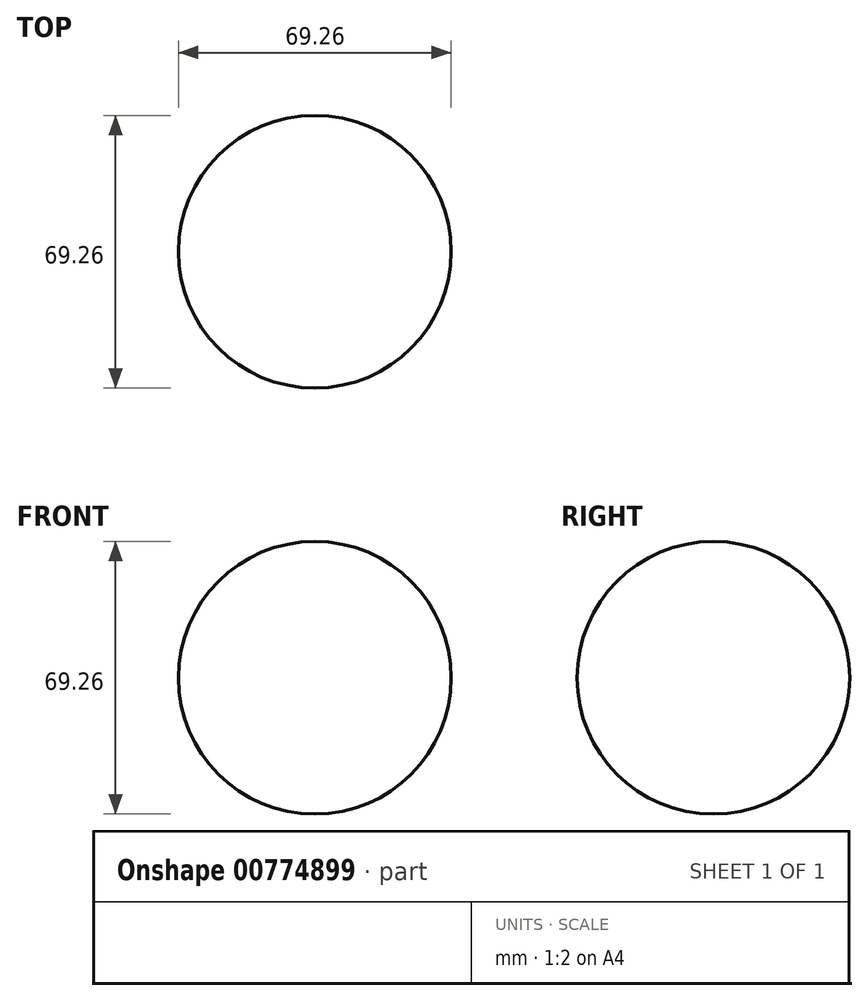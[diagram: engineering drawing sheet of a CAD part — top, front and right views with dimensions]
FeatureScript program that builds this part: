
annotation { "Feature Type Name" : "Feature", "Feature Type Description" : "" }
export const myFeature = defineFeature(function(context is Context, id is Id, definition is map)
    precondition{}
    {
        {
            var Q0;
            Q0=qCreatedBy(makeId("Front.planeOp"),FACE);
            var sketch = newSketch(context, id + "F0", { "sketchPlane" : qUnion([Q0])});
            skCircle(sketch, "E0", {"center": v(0, 0) * mm, "radius": 34.63 * mm});
            skLineSegment(sketch, "E1", {"start": v(0, 34.63) * mm, "end": v(0, -34.63) * mm});
            skSolve(sketch);
        }
        {
            var Q0;
            {var subQ0=sQuery(id+"F0.wireOp",EDGE,"E1");Q0=makeQuery(id+"F0.imprint","IMPRINT",FACE,{"disambiguationData":[TD([[makeQuery(id+"F0.imprint","IMPRINT",EDGE,{"derivedFrom":subQ0}),1.0]])]});}
            var Q1;
            Q1=sQuery(id+"F0.wireOp",EDGE,"E1");
            revolve(context, id + "F1", {"surfaceOperationType" : NewSurfaceOperationType.NEW, "entities" : qUnion([Q0]), "axis" : qUnion([Q1]), "revolveType" : RevolveType.FULL});
        }
    });
